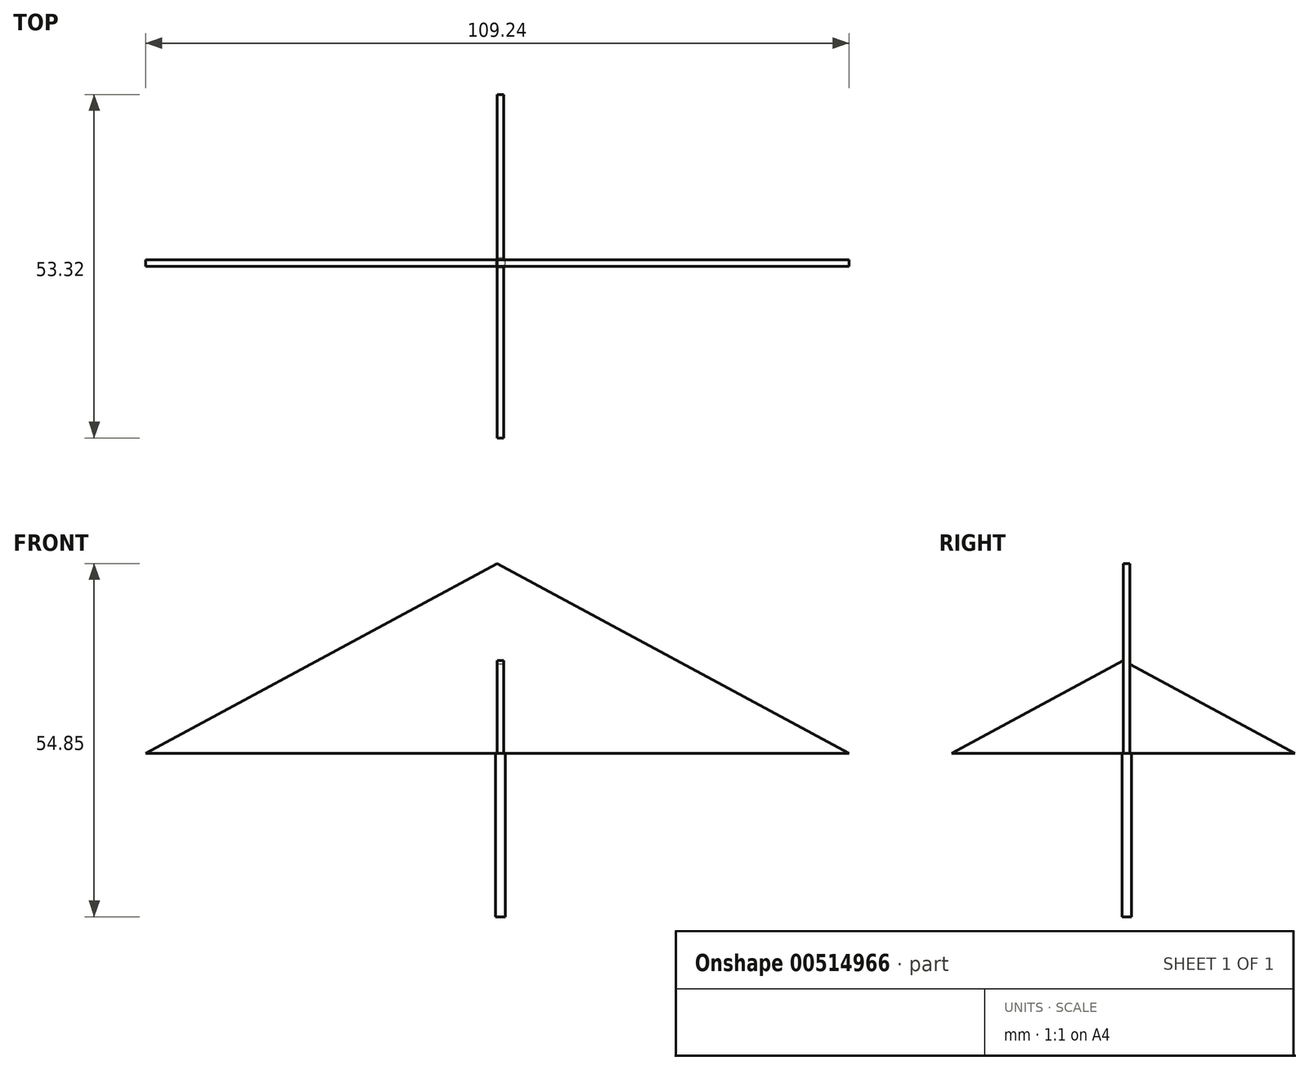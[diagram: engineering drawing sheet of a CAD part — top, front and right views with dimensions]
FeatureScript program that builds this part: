
annotation { "Feature Type Name" : "Feature", "Feature Type Description" : "" }
export const myFeature = defineFeature(function(context is Context, id is Id, definition is map)
    precondition{}
    {
        {
            var Q0;
            Q0=qCreatedBy(makeId("Front.planeOp"),FACE);
            var sketch = newSketch(context, id + "F0", { "sketchPlane" : qUnion([Q0])});
            skLineSegment(sketch, "E0", {"start": v(0, 0) * mm, "end": v(0, 29.45) * mm});
            skLineSegment(sketch, "E1", {"start": v(0, 29.45) * mm, "end": v(-54.62, 0) * mm});
            skLineSegment(sketch, "E2", {"start": v(0, 0) * mm, "end": v(-54.62, 0) * mm});
            skLineSegment(sketch, "E3.MirrorCS", {"start": v(0, 29.45) * mm, "end": v(54.62, 0) * mm});
            skLineSegment(sketch, "E4.MirrorCS", {"start": v(0, 0) * mm, "end": v(54.62, 0) * mm});
            skSolve(sketch);
        }
        {
            var Q0;
            Q0=qCreatedBy(makeId("Right.planeOp"),FACE);
            var sketch = newSketch(context, id + "F1", { "sketchPlane" : qUnion([Q0])});
            skLineSegment(sketch, "E5", {"start": v(0, 0) * mm, "end": v(0, 14.36) * mm});
            skLineSegment(sketch, "E6", {"start": v(0, 14.36) * mm, "end": v(-26.66, 0) * mm});
            skLineSegment(sketch, "E7", {"start": v(-26.66, 0) * mm, "end": v(0, 0) * mm});
            skLineSegment(sketch, "E8.MirrorCS", {"start": v(0, 14.36) * mm, "end": v(26.66, 0) * mm});
            skLineSegment(sketch, "E9.MirrorCS", {"start": v(26.66, 0) * mm, "end": v(0, 0) * mm});
            skSolve(sketch);
        }
        {
            var Q0;
            Q0=makeQuery(id+"F0.imprint","IMPRINT",FACE,{"disambiguationData":[TD([[makeQuery(id+"F0.imprint","IMPRINT",EDGE,{"derivedFrom":sQuery(id+"F0.wireOp",EDGE,"E0")}),1.0]])]});
            var Q1;
            Q1=makeQuery(id+"F0.imprint","IMPRINT",FACE,{"disambiguationData":[TD([[makeQuery(id+"F0.imprint","IMPRINT",EDGE,{"derivedFrom":sQuery(id+"F0.wireOp",EDGE,"E0")}),-1.0]])]});
            extrude(context, id + "F2", {"entities" : qUnion([Q0, Q1]), "oppositeDirection" : true, "depth" : 1 * mm, "offsetDistance" : 25.4 * mm});
        }
        {
            var Q0;
            Q0=makeQuery(id+"F1.imprint","IMPRINT",FACE,{"disambiguationData":[TD([[makeQuery(id+"F1.imprint","IMPRINT",EDGE,{"derivedFrom":sQuery(id+"F1.wireOp",EDGE,"E5")}),-1.0]])]});
            var Q1;
            Q1=makeQuery(id+"F1.imprint","IMPRINT",FACE,{"disambiguationData":[TD([[makeQuery(id+"F1.imprint","IMPRINT",EDGE,{"derivedFrom":sQuery(id+"F1.wireOp",EDGE,"E5")}),1.0]])]});
            var Q2;
            Q2=sQuery(id+"F1.wireOp",EDGE,"E6");
            extrude(context, id + "F3", {"entities" : qUnion([Q0, Q1]), "operationType" : NewBodyOperationType.ADD, "surfaceEntities" : qUnion([Q2]), "depth" : 1 * mm, "offsetDistance" : 25.4 * mm});
        }
        {
            var Q0;
            Q0=qCreatedBy(makeId("Top.planeOp"),FACE);
            var sketch = newSketch(context, id + "F4", { "sketchPlane" : qUnion([Q0])});
            skCircle(sketch, "E10", {"center": v(0.49, 0.53) * mm, "radius": 0.75 * mm});
            skSolve(sketch);
        }
        {
            var Q0;
            Q0=makeQuery(id+"F4.imprint","IMPRINT",FACE,{"disambiguationData":[TD([[makeQuery(id+"F4.imprint","IMPRINT",EDGE,{"derivedFrom":sQuery(id+"F4.wireOp",EDGE,"E10")}),1.0]])]});
            extrude(context, id + "F5", {"entities" : qUnion([Q0]), "operationType" : NewBodyOperationType.ADD, "oppositeDirection" : true, "depth" : 25.4 * mm, "offsetDistance" : 25.4 * mm});
        }
    });
